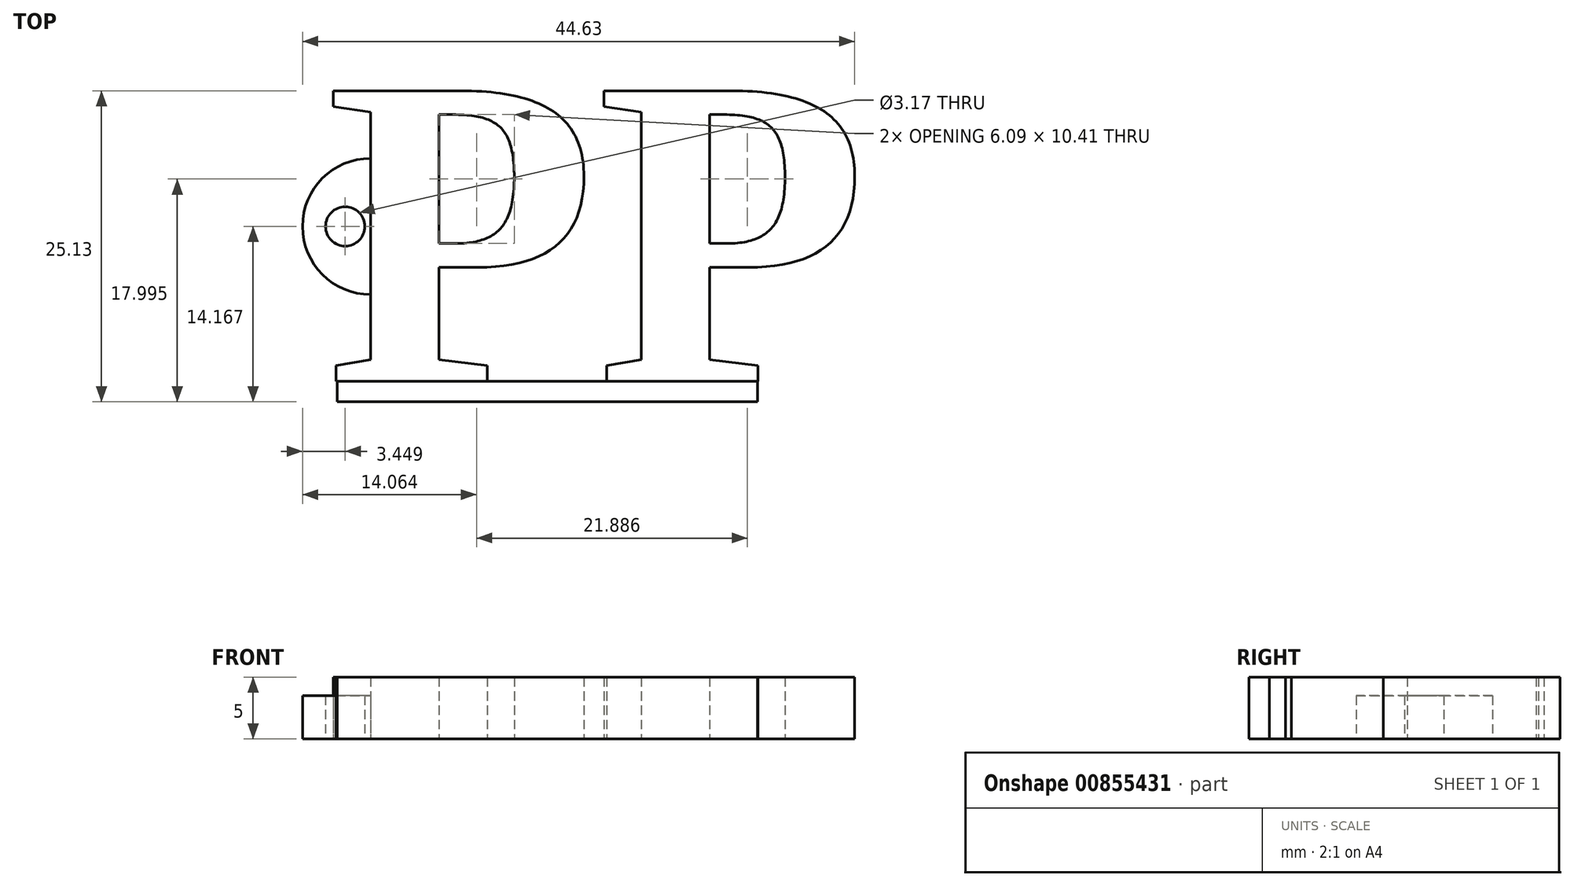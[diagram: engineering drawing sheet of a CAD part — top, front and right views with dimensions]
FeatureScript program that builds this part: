
annotation { "Feature Type Name" : "Feature", "Feature Type Description" : "" }
export const myFeature = defineFeature(function(context is Context, id is Id, definition is map)
    precondition{}
    {
        {
            var Q0;
            Q0=qCreatedBy(makeId("Top.planeOp"),FACE);
            var sketch = newSketch(context, id + "F0", { "sketchPlane" : qUnion([Q0])});
            skText(sketch, "E0", { "text": "PP", "fontName": "Tinos-Bold.ttf"});
            skLineSegment(sketch, "E1.bottom", {"start": v(-27.18, 1.75) * mm, "end": v(6.81, 1.75) * mm});
            skLineSegment(sketch, "E1.top", {"start": v(-27.18, 0.09) * mm, "end": v(6.81, 0.09) * mm});
            skLineSegment(sketch, "E1.left", {"start": v(-27.18, 1.75) * mm, "end": v(-27.18, 0.09) * mm});
            skLineSegment(sketch, "E1.right", {"start": v(6.81, 1.75) * mm, "end": v(6.81, 0.09) * mm});
            skCircle(sketch, "E2", {"center": v(-24.47, 14.26) * mm, "radius": 5.5 * mm});
            skCircle(sketch, "E3", {"center": v(-26.52, 14.26) * mm, "radius": 1.59 * mm});
            const initialGuessF0  = {"E0": [-0.0281, 0.00175, 1, 0, 0.0258]};
            skSetInitialGuess(sketch, initialGuessF0);
            skSolve(sketch);
        }
        {
            var Q0;
            Q0=makeQuery(id+"F0.imprint","IMPRINT",FACE,{"disambiguationData":[TD([[makeQuery(id+"F0.imprint","IMPRINT",EDGE,{"derivedFrom":sQuery(id+"F0.wireOp",EDGE,"E0.sketch_text.stroke-0")}),-1.0]])]});
            var Q1;
            Q1=makeQuery(id+"F0.imprint","IMPRINT",FACE,{"disambiguationData":[TD([[makeQuery(id+"F0.imprint","IMPRINT",EDGE,{"derivedFrom":sQuery(id+"F0.wireOp",EDGE,"E0.sketch_text.stroke-21")}),-1.0]])]});
            var Q2;
            {var subQ0=sQuery(id+"F0.wireOp",EDGE,"E2");var subQ1=sQuery(id+"F0.wireOp",EDGE,"E0.sketch_text.stroke-13");var subQ2=makeQuery(id+"F0.imprint","INTERSECT",VERTEX,{"disambiguationData":[OD(0.0)],"derivedFrom":[subQ1,subQ0]});Q2=makeQuery(id+"F0.imprint","IMPRINT",FACE,{"disambiguationData":[TD([[makeQuery(id+"F0.imprint","IMPRINT",EDGE,{"disambiguationData":[TD([[subQ2,-1.0]])],"derivedFrom":subQ1}),-1.0]])]});}
            var Q3;
            Q3=makeQuery(id+"F0.imprint","IMPRINT",FACE,{"disambiguationData":[TD([[makeQuery(id+"F0.imprint","IMPRINT",EDGE,{"derivedFrom":sQuery(id+"F0.wireOp",EDGE,"E1.top")}),1.0]])]});
            extrude(context, id + "F1", {"entities" : qUnion([Q0, Q1, Q2, Q3]), "depth" : 5 * mm, "offsetDistance" : 25 * mm});
        }
        {
            var Q0;
            Q0=makeQuery(id+"F0.imprint","IMPRINT",FACE,{"disambiguationData":[TD([[makeQuery(id+"F0.imprint","IMPRINT",EDGE,{"derivedFrom":sQuery(id+"F0.wireOp",EDGE,"E3")}),-1.0]])]});
            extrude(context, id + "F2", {"entities" : qUnion([Q0]), "operationType" : NewBodyOperationType.ADD, "depth" : 3.5 * mm, "offsetDistance" : 25 * mm});
        }
    });
